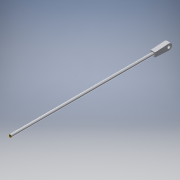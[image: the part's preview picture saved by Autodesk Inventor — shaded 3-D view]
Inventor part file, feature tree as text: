
AUTODESK INVENTOR PART (.ipt)
format: ipt  version: 2016 (Build 200138000, 138)  size: 141,824 bytes
history: native  units: mm
features: sketch x7, extrude x5, hole x1, thread x1, revolve x1
ambient origin geometry x8: Origin, YZ Plane, XZ Plane, XY Plane, X Axis, Y Axis, Z Axis, Center Point
bodies: Solid1 (feature_tree)
feature tree (15):
  extrude  "Extrusion1"  Depth=433.3875mm TaperAngle=0.0deg
  extrude  "Extrusion2"  Depth=13.0mm
  extrude  "Extrusion3"  Depth=18.0mm
  extrude  "Extrusion4"  Depth=9.0mm
  extrude  "Extrusion5"  Depth=20.0mm
  hole  "Hole2"  [1 undecoded]
  thread  "Thread2"  [1 undecoded]
  revolve  "Revolution1"  [1 undecoded]
  sketch  "Sketch1"  dims[d0=8.0mm d1=433.3875mm d2=0.0mm]
  sketch  "Sketch2"  dims[d3=13.0mm d4=13.0mm]
  sketch  "Sketch3"  dims[d5=41.0mm d6=0.0mm d7=18.0mm]
  sketch  "Sketch4"  dims[d8=13.0mm d9=0.0mm d11=9.0mm]
  sketch  "Sketch5"  dims[d12=15.0mm d13=0.0mm d25=20.0mm]
  sketch  "Sketch6"  dims[d26=1.0mm d27=15.0mm d28=0.0mm d29=32.0mm]
  sketch  "Sketch7"  dims[d30=3.0mm d31=6.0mm d32=4.0mm d33=2.0mm d34=90.0deg d35=10.0mm d36=20.594885mm d37=10.0mm d38=0.0mm d41=12.7mm d43=1.8mm d44=90.0deg]
note: 3 required parameter values undecoded (feature->parameter linkage not recoverable at this tier; creation-order binding heuristic only, values carry confidence <= 0.55)